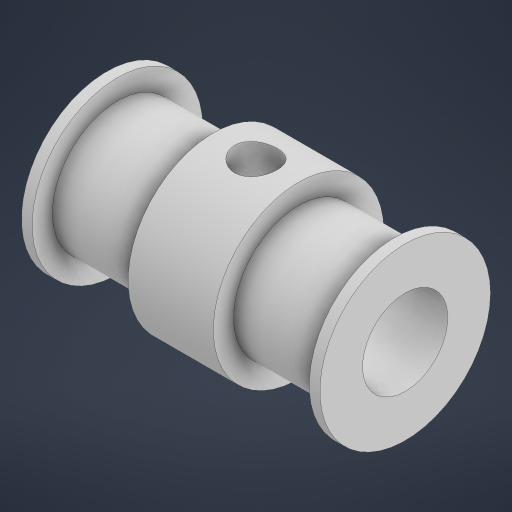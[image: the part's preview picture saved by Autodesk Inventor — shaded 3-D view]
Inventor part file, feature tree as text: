
AUTODESK INVENTOR PART (.ipt)
format: ipt  version: 2024 (Build 280153000, 153)  size: 261,120 bytes
history: native  units: mm
features: sketch x3, other x2, extrude x2, revolve x1, pattern_circular x1
ambient origin geometry x8: Origin, YZ Plane, XZ Plane, XY Plane, X Axis, Y Axis, Z Axis, Center Point
bodies: Body1 (feature_tree)
feature tree (9):
  other  "Твердое тело1"
  revolve  "Вращение1"
  extrude  "Выдавливание1"  Depth=6.11mm
  other  "РабПлоскость1"
  extrude  "Выдавливание2"  Depth=8.0mm
  pattern_circular  "Круговой массив1"  [2 undecoded]
  sketch  "Эскиз1"
  sketch  "Эскиз2"
  sketch  "Эскиз3"
note: 2 required parameter values undecoded (feature->parameter linkage not recoverable at this tier; creation-order binding heuristic only, values carry confidence <= 0.55)
